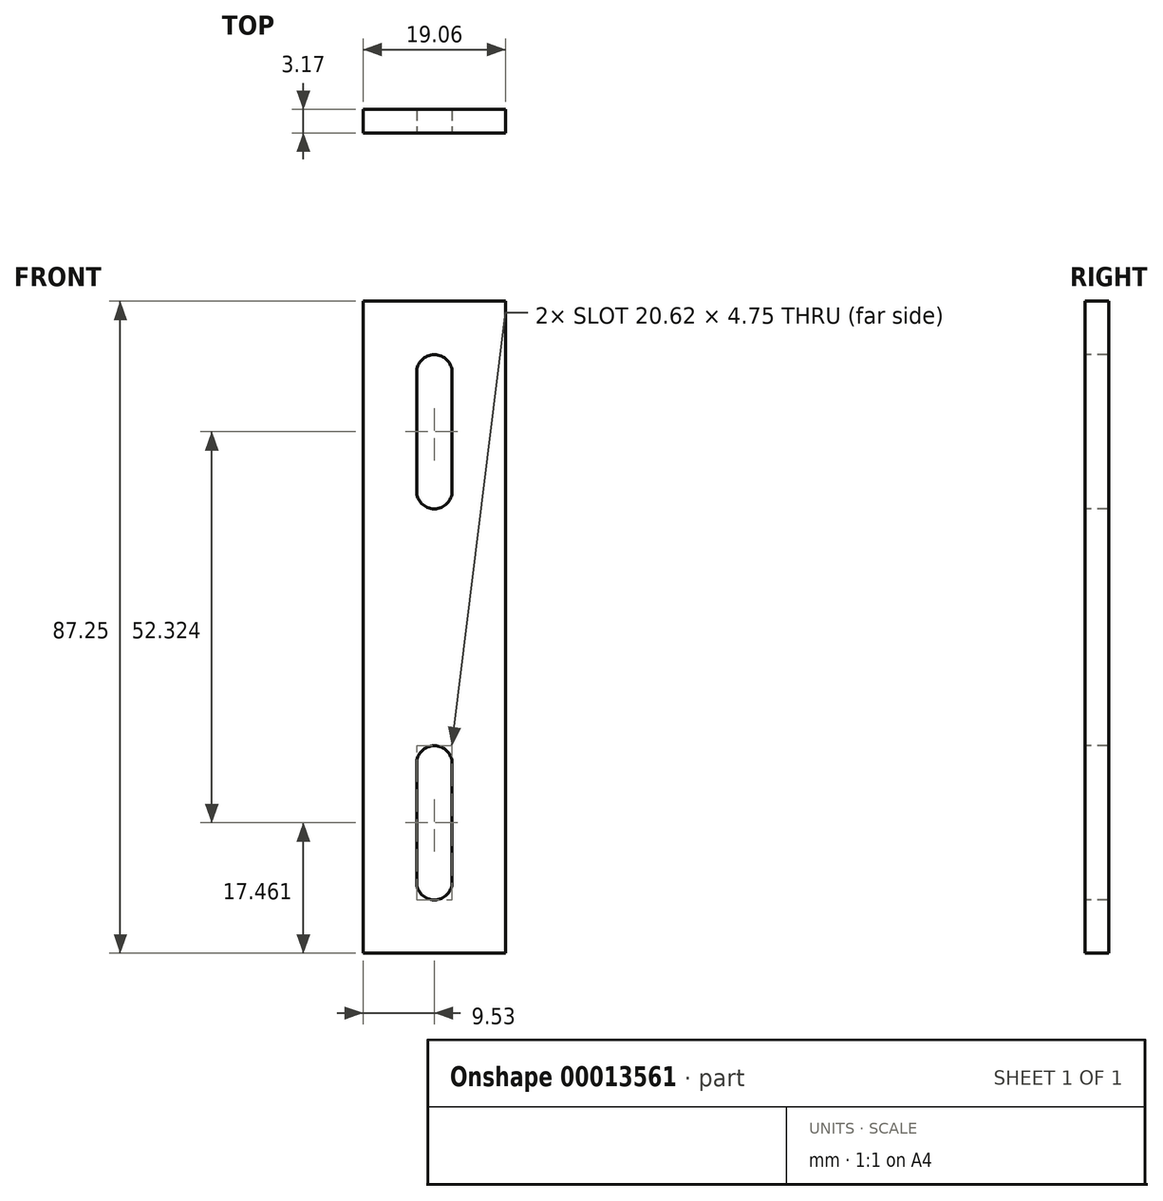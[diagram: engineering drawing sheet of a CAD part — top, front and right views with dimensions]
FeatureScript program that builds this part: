
annotation { "Feature Type Name" : "Feature", "Feature Type Description" : "" }
export const myFeature = defineFeature(function(context is Context, id is Id, definition is map)
    precondition{}
    {
        {
            var Q0;
            Q0=qCreatedBy(makeId("Front.planeOp"),FACE);
            var sketch = newSketch(context, id + "F0", { "sketchPlane" : qUnion([Q0])});
            skLineSegment(sketch, "E0.bottom", {"start": v(-9.53, 43.64) * mm, "end": v(9.52, 43.64) * mm});
            skLineSegment(sketch, "E0.top", {"start": v(-9.52, -43.61) * mm, "end": v(9.53, -43.61) * mm});
            skLineSegment(sketch, "E0.left", {"start": v(-9.53, 43.64) * mm, "end": v(-9.52, -43.61) * mm});
            skLineSegment(sketch, "E0.right", {"start": v(9.52, 43.64) * mm, "end": v(9.53, -43.61) * mm});
            skPoint(sketch, "E1", {"position": v(0, -26.16) * mm});
            skPoint(sketch, "E2", {"position": v(0, 0) * mm});
            skPoint(sketch, "E3", {"position": v(0, 26.16) * mm});
            skLineSegment(sketch, "E4", {"start": v(0, 34.11) * mm, "end": v(0, 18.24) * mm});
            skArc(sketch, "E5.0.startCap", {"start": v(-2.37, 34.11) * mm, "mid": v(0, 36.49) * mm, "end": v(2.37, 34.11) * mm});
            skArc(sketch, "E5.0.endCap", {"start": v(2.37, 18.24) * mm, "mid": v(0, 15.86) * mm, "end": v(-2.37, 18.24) * mm});
            skLineSegment(sketch, "E5.0.left", {"start": v(2.37, 34.11) * mm, "end": v(2.37, 18.24) * mm});
            skLineSegment(sketch, "E5.0.right", {"start": v(-2.37, 34.11) * mm, "end": v(-2.37, 18.24) * mm});
            skLineSegment(sketch, "E6", {"start": v(0, -18.21) * mm, "end": v(0, -34.09) * mm});
            skArc(sketch, "E7.0.startCap", {"start": v(-2.37, -18.21) * mm, "mid": v(0, -15.84) * mm, "end": v(2.37, -18.21) * mm});
            skArc(sketch, "E7.0.endCap", {"start": v(2.37, -34.09) * mm, "mid": v(0, -36.46) * mm, "end": v(-2.37, -34.09) * mm});
            skLineSegment(sketch, "E7.0.left", {"start": v(2.37, -18.21) * mm, "end": v(2.37, -34.09) * mm});
            skLineSegment(sketch, "E7.0.right", {"start": v(-2.37, -18.21) * mm, "end": v(-2.37, -34.09) * mm});
            skSolve(sketch);
        }
        {
            var Q0;
            Q0=makeQuery(id+"F0.imprint","IMPRINT",FACE,{"disambiguationData":[TD([[makeQuery(id+"F0.imprint","IMPRINT",EDGE,{"derivedFrom":sQuery(id+"F0.wireOp",EDGE,"E0.bottom")}),-1.0]])]});
            extrude(context, id + "F1", {"entities" : qUnion([Q0]), "oppositeDirection" : true, "depth" : 3.17 * mm});
        }
    });
